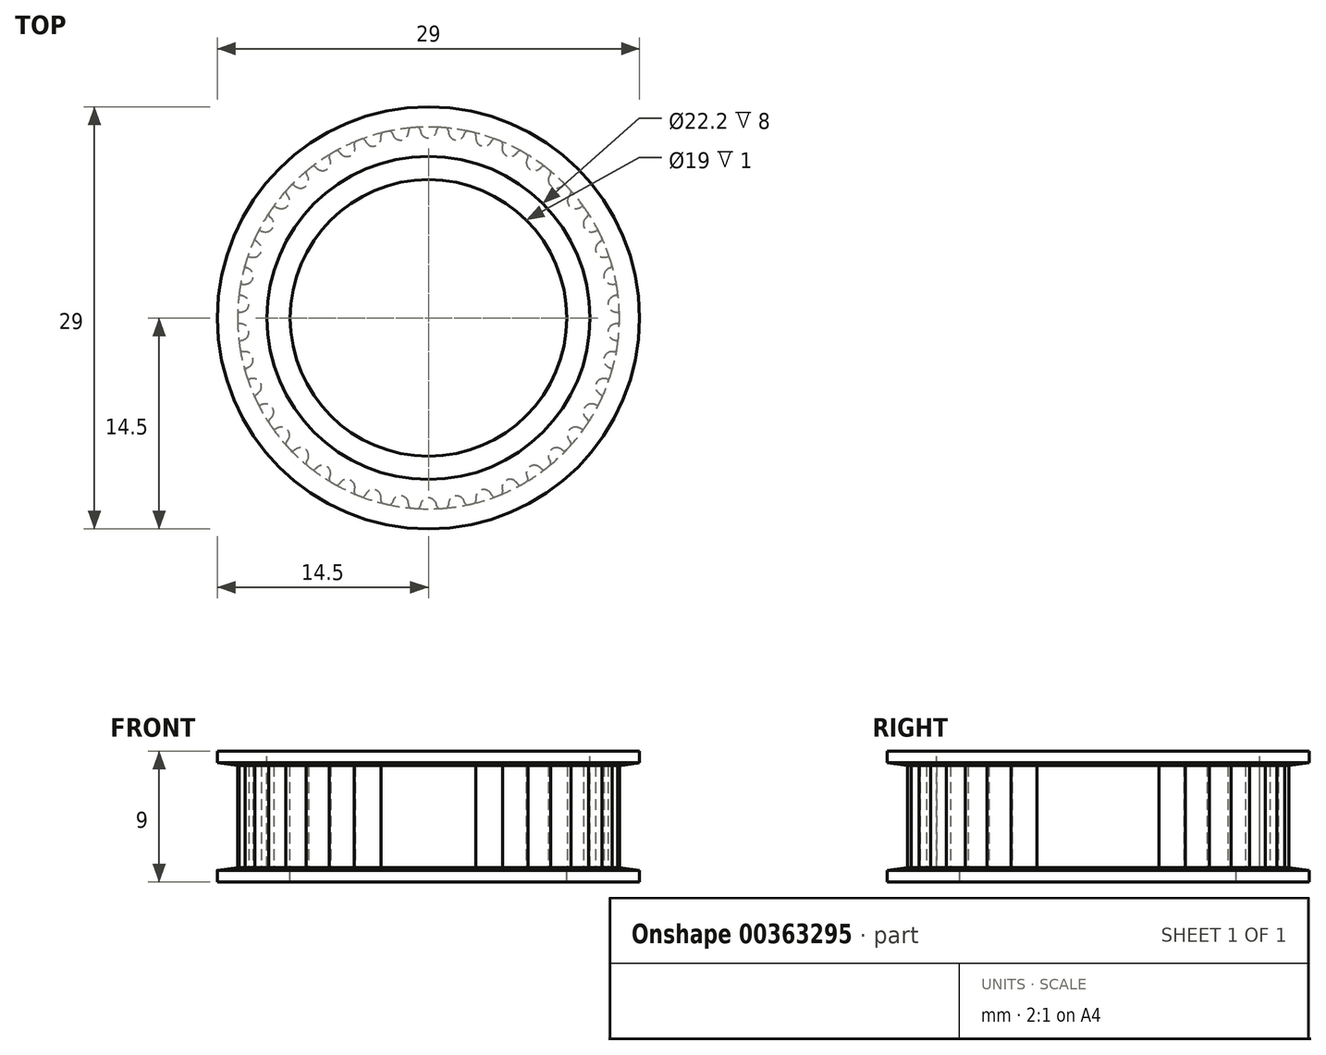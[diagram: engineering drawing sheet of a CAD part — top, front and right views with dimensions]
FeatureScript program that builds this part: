
annotation { "Feature Type Name" : "Feature", "Feature Type Description" : "" }
export const myFeature = defineFeature(function(context is Context, id is Id, definition is map)
    precondition{}
    {
        {
            assignVariable(context, id + "F0", {"name" : "teeth", "anyValue" : 42});
        }
        {
            assignVariable(context, id + "F1", {"name" : "belt_width", "anyValue" : 7});
        }
        {
            var Q0;
            Q0=qCreatedBy(makeId("Top.planeOp"),FACE);
            var sketch = newSketch(context, id + "F2", { "sketchPlane" : qUnion([Q0])});
            skLineSegment(sketch, "E0", {"start": v(0, 0) * mm, "end": v(0, 12.37) * mm, "construction": true});
            skCircle(sketch, "E1", {"center": v(0, 0) * mm, "radius": 13.12 * mm});
            skPoint(sketch, "E2.MirrorCS.end.orphan", {"position": v(0.98, 13.08) * mm});
            skLineSegment(sketch, "E3", {"start": v(0.98, 13.08) * mm, "end": v(1, 13.33) * mm, "construction": true});
            skLineSegment(sketch, "E4", {"start": v(-0.98, 13.08) * mm, "end": v(-1, 13.33) * mm, "construction": true});
            skArc(sketch, "E5", {"start": v(0, 12.37) * mm, "mid": v(0.34, 12.48) * mm, "end": v(0.54, 12.77) * mm});
            skArc(sketch, "E6", {"start": v(0.54, 12.77) * mm, "mid": v(0.56, 12.87) * mm, "end": v(0.58, 12.97) * mm, "construction": true});
            skLineSegment(sketch, "E7", {"start": v(0, 12.37) * mm, "end": v(0, 13.12) * mm, "construction": true});
            skLineSegment(sketch, "E8", {"start": v(0, 13.12) * mm, "end": v(0, 13.37) * mm, "construction": true});
            skArc(sketch, "E9", {"start": v(0.58, 12.97) * mm, "mid": v(0.64, 13.06) * mm, "end": v(0.74, 13.1) * mm, "construction": true});
            skArc(sketch, "E10", {"start": v(1, 13.33) * mm, "mid": v(0, 13.37) * mm, "end": v(-1, 13.33) * mm, "construction": true});
            skLineSegment(sketch, "E11", {"start": v(0.98, 13.08) * mm, "end": v(0.92, 12.33) * mm});
            skLineSegment(sketch, "E12", {"start": v(0.92, 12.33) * mm, "end": v(0, 0) * mm});
            skLineSegment(sketch, "E13", {"start": v(0, 0) * mm, "end": v(-0.92, 12.33) * mm});
            skLineSegment(sketch, "E14", {"start": v(-0.92, 12.33) * mm, "end": v(-0.98, 13.08) * mm});
            skArc(sketch, "E15", {"start": v(0.77, 13.1) * mm, "mid": v(0.65, 13.06) * mm, "end": v(0.58, 12.95) * mm});
            skArc(sketch, "E16", {"start": v(0.54, 12.77) * mm, "mid": v(0.56, 12.86) * mm, "end": v(0.58, 12.95) * mm});
            skArc(sketch, "E17.MirrorCS", {"start": v(0, 12.37) * mm, "mid": v(-0.34, 12.48) * mm, "end": v(-0.54, 12.77) * mm});
            skArc(sketch, "E18.MirrorCS", {"start": v(-0.54, 12.77) * mm, "mid": v(-0.56, 12.86) * mm, "end": v(-0.58, 12.95) * mm});
            skArc(sketch, "E19.MirrorCS", {"start": v(-0.77, 13.1) * mm, "mid": v(-0.65, 13.06) * mm, "end": v(-0.58, 12.95) * mm});
            skArc(sketch, "E20", {"start": v(0, 13.12) * mm, "mid": v(-0.2, 13.11) * mm, "end": v(-0.4, 13.1) * mm});
            skArc(sketch, "E21", {"start": v(0.92, 12.33) * mm, "mid": v(0, 12.37) * mm, "end": v(-0.92, 12.33) * mm, "construction": true});
            skLineSegment(sketch, "E22", {"start": v(1, 13.33) * mm, "end": v(1.03, 13.7) * mm, "construction": true});
            skLineSegment(sketch, "E23", {"start": v(-1, 13.33) * mm, "end": v(-1.03, 13.7) * mm, "construction": true});
            skArc(sketch, "E24", {"start": v(-1.03, 13.7) * mm, "mid": v(0, 13.75) * mm, "end": v(1.03, 13.7) * mm, "construction": true});
            skSolve(sketch);
        }
        {
            var Q0;
            Q0=makeQuery(id+"F2.imprint","IMPRINT",FACE,{"disambiguationData":[TD([[makeQuery(id+"F2.imprint","IMPRINT",EDGE,{"derivedFrom":sQuery(id+"F2.wireOp",EDGE,"E5")}),-1.0]])]});
            var Q1;
            {var subQ1=sQuery(id+"F2.wireOp",EDGE,"E14");Q1=makeQuery(id+"F2.imprint","IMPRINT",FACE,{"disambiguationData":[TD([[makeQuery(id+"F2.imprint","IMPRINT",EDGE,{"derivedFrom":subQ1}),-1.0]])]});}
            var Q2;
            {var subQ0=sQuery(id+"F2.wireOp",EDGE,"E12");Q2=makeQuery(id+"F2.imprint","IMPRINT",FACE,{"disambiguationData":[TD([[makeQuery(id+"F2.imprint","IMPRINT",EDGE,{"derivedFrom":subQ0}),-1.0]])]});}
            extrude(context, id + "F3", {"entities" : qUnion([Q0, Q1, Q2]), "endBound" : BoundingType.SYMMETRIC, "depth" : (getVariable(context, 'belt_width')) * mm});
        }
        {
            var Q0;
            Q0=makeQuery(id+"F3.opExtrude","SWEPT_BODY",BODY,{"disambiguationData":[OSD([sQuery(id+"F2.wireOp",EDGE,"E1"),sQuery(id+"F2.wireOp",EDGE,"E5"),sQuery(id+"F2.wireOp",EDGE,"E11"),sQuery(id+"F2.wireOp",EDGE,"E12"),sQuery(id+"F2.wireOp",EDGE,"E13"),sQuery(id+"F2.wireOp",EDGE,"E14"),sQuery(id+"F2.wireOp",EDGE,"E15"),sQuery(id+"F2.wireOp",EDGE,"E16"),sQuery(id+"F2.wireOp",EDGE,"E17.MirrorCS"),sQuery(id+"F2.wireOp",EDGE,"E18.MirrorCS"),sQuery(id+"F2.wireOp",EDGE,"E19.MirrorCS")])]});
            var Q1;
            Q1=makeQuery(id+"F3.opExtrude","SWEPT_EDGE",EDGE,{"disambiguationData":[OSD([sQuery(id+"F2.wireOp",EDGE,"E12"),sQuery(id+"F2.wireOp",EDGE,"E13")])]});
            circularPattern(context, id + "F4", {"operationType" : NewBodyOperationType.ADD, "entities" : qUnion([Q0]), "axis" : qUnion([Q1]), "angle" : 360 * degree, "instanceCount" : getVariable(context, 'teeth'), "equalSpace" : true});
        }
        {
            var Q0;
            Q0=qCreatedBy(makeId("Front.planeOp"),FACE);
            var sketch = newSketch(context, id + "F5", { "sketchPlane" : qUnion([Q0])});
            skLineSegment(sketch, "E25", {"start": v(0, -3.5) * mm, "end": v(13.12, -3.5) * mm});
            skLineSegment(sketch, "E26", {"start": v(13.12, -3.5) * mm, "end": v(14.5, -3.7) * mm});
            skLineSegment(sketch, "E27", {"start": v(0, 3.5) * mm, "end": v(13.12, 3.5) * mm});
            skLineSegment(sketch, "E28", {"start": v(14.5, 3.7) * mm, "end": v(13.12, 3.5) * mm});
            skLineSegment(sketch, "E29", {"start": v(14.5, 3.7) * mm, "end": v(14.5, 4.5) * mm});
            skLineSegment(sketch, "E30", {"start": v(14.5, 4.5) * mm, "end": v(0, 4.5) * mm});
            skLineSegment(sketch, "E31", {"start": v(0, 4.5) * mm, "end": v(0, 3.5) * mm});
            skLineSegment(sketch, "E32", {"start": v(13.12, -3.5) * mm, "end": v(14.5, -3.5) * mm, "construction": true});
            skLineSegment(sketch, "E33", {"start": v(14.5, -3.5) * mm, "end": v(14.5, -3.7) * mm, "construction": true});
            skLineSegment(sketch, "E34", {"start": v(13.12, 3.5) * mm, "end": v(14.5, 3.5) * mm, "construction": true});
            skLineSegment(sketch, "E35", {"start": v(14.5, 3.5) * mm, "end": v(14.5, 3.7) * mm, "construction": true});
            skLineSegment(sketch, "E36", {"start": v(13.12, 0) * mm, "end": v(13.12, -3.5) * mm, "construction": true});
            skLineSegment(sketch, "E37", {"start": v(14.5, -4.5) * mm, "end": v(0, -4.5) * mm});
            skLineSegment(sketch, "E38", {"start": v(14.5, -3.7) * mm, "end": v(14.5, -4.5) * mm});
            skLineSegment(sketch, "E39", {"start": v(0, -3.5) * mm, "end": v(0, -4.5) * mm});
            skLineSegment(sketch, "E40", {"start": v(0, 4.5) * mm, "end": v(0, -4.5) * mm, "construction": true});
            skSolve(sketch);
        }
        {
            var Q0;
            Q0=makeQuery(id+"F5.imprint","IMPRINT",FACE,{"disambiguationData":[TD([[makeQuery(id+"F5.imprint","IMPRINT",EDGE,{"derivedFrom":sQuery(id+"F5.wireOp",EDGE,"E25")}),-1.0]])]});
            var Q1;
            Q1=makeQuery(id+"F5.imprint","IMPRINT",FACE,{"disambiguationData":[TD([[makeQuery(id+"F5.imprint","IMPRINT",EDGE,{"derivedFrom":sQuery(id+"F5.wireOp",EDGE,"E27")}),1.0]])]});
            var Q2;
            Q2=qConstructionFilter(qBodyType(qCreatedBy(id+"F5",EDGE),BodyType.WIRE),ConstructionObject.NO);
            var Q3;
            Q3=sQuery(id+"F5.wireOp",EDGE,"E40");
            revolve(context, id + "F6", {"operationType" : NewBodyOperationType.ADD, "entities" : qUnion([Q0, Q1]), "surfaceEntities" : qUnion([Q2]), "axis" : qUnion([Q3]), "revolveType" : RevolveType.FULL});
        }
        {
            var Q0;
            Q0=makeQuery(id+"F6.opRevolve","SWEPT_FACE",FACE,{"disambiguationData":[OSD([sQuery(id+"F5.wireOp",EDGE,"E30")])]});
            var sketch = newSketch(context, id + "F7", { "sketchPlane" : qUnion([Q0])});
            skPoint(sketch, "E41", {"position": v(0, 0) * mm});
            skCircle(sketch, "E42", {"center": v(0, 0) * mm, "radius": 11.1 * mm});
            skCircle(sketch, "E43", {"center": v(0, 0) * mm, "radius": 9.5 * mm});
            skSolve(sketch);
        }
        {
            var Q0;
            Q0=makeQuery(id+"F7.imprint","IMPRINT",FACE,{"disambiguationData":[TD([[makeQuery(id+"F7.imprint","IMPRINT",EDGE,{"derivedFrom":sQuery(id+"F7.wireOp",EDGE,"E42")}),1.0]])]});
            extrude(context, id + "F8", {"entities" : qUnion([Q0]), "operationType" : NewBodyOperationType.REMOVE, "oppositeDirection" : true, "depth" : 8 * mm});
        }
        {
            var Q0;
            Q0=makeQuery(id+"F8.boolean.opBoolean","SPLIT",FACE,{"disambiguationData":[TD([makeQuery(id+"F8.opExtrude","SWEPT_FACE",FACE,{"disambiguationData":[OSD([sQuery(id+"F7.wireOp",EDGE,"E43")])]})])],"derivedFrom":makeQuery(id+"F6.opRevolve","SWEPT_FACE",FACE,{"disambiguationData":[OSD([sQuery(id+"F5.wireOp",EDGE,"E30")])]})});
            extrude(context, id + "F9", {"entities" : qUnion([Q0]), "operationType" : NewBodyOperationType.REMOVE, "endBound" : BoundingType.UP_TO_NEXT, "oppositeDirection" : true, "depth" : 25 * mm});
        }
    });
